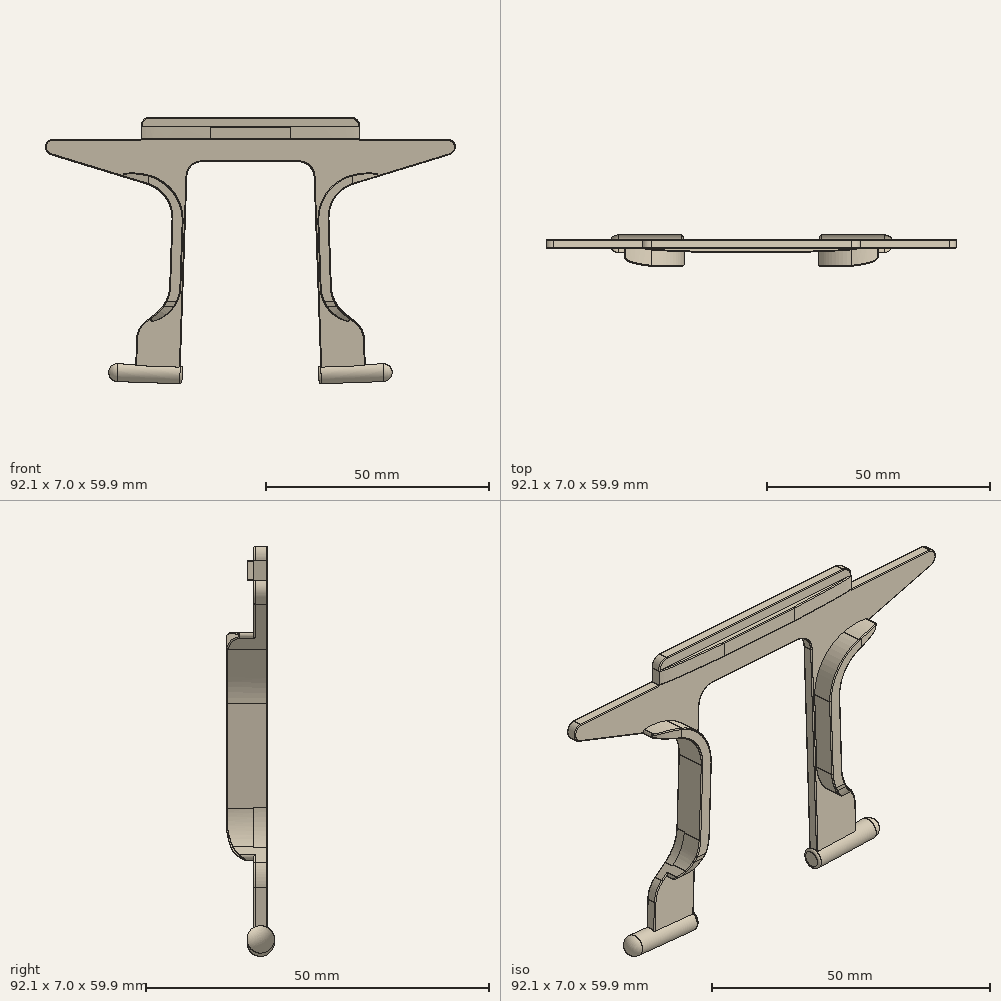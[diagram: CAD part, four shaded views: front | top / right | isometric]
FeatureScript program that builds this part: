
annotation { "Feature Type Name" : "Feature", "Feature Type Description" : "" }
export const myFeature = defineFeature(function(context is Context, id is Id, definition is map)
    precondition{}
    {
        {
            var Q0;
            Q0=qCreatedBy(makeId("Front.planeOp"),FACE);
            var sketch = newSketch(context, id + "F0", { "sketchPlane" : qUnion([Q0])});
            skLineSegment(sketch, "E0", {"start": v(24.5, 40.36) * mm, "end": v(44.5, 40.36) * mm});
            skLineSegment(sketch, "E1", {"start": v(0, 45.36) * mm, "end": v(22.5, 45.36) * mm});
            skLineSegment(sketch, "E2", {"start": v(24.5, 43.36) * mm, "end": v(24.5, 40.36) * mm});
            skPoint(sketch, "E3.visualSharp", {"position": v(24.5, 45.36) * mm});
            skArc(sketch, "E3.filletArc", {"start": v(24.5, 43.36) * mm, "mid": v(23.91, 44.77) * mm, "end": v(22.5, 45.36) * mm});
            skArc(sketch, "E4", {"start": v(44.8, 36.95) * mm, "mid": v(46, 38.99) * mm, "end": v(44.07, 40.36) * mm});
            skLineSegment(sketch, "E5", {"start": v(15.84, -12.5) * mm, "end": v(14.29, 31.98) * mm});
            skLineSegment(sketch, "E6", {"start": v(10.79, 35.36) * mm, "end": v(0, 35.36) * mm});
            skLineSegment(sketch, "E7", {"start": v(44.8, 36.95) * mm, "end": v(23.28, 30.37) * mm});
            skLineSegment(sketch, "E8", {"start": v(25.83, -12.14) * mm, "end": v(25.56, -4.43) * mm});
            skPoint(sketch, "E9.visualSharp", {"position": v(14.17, 35.36) * mm});
            skArc(sketch, "E9.filletArc", {"start": v(14.29, 31.98) * mm, "mid": v(13.22, 34.38) * mm, "end": v(10.79, 35.36) * mm});
            skLineSegment(sketch, "E10", {"start": v(25.83, -12.14) * mm, "end": v(15.84, -12.5) * mm});
            skPoint(sketch, "E11.MirrorCS.start.orphan", {"position": v(0, 45.36) * mm});
            skPoint(sketch, "E12.MirrorCS.end.orphan", {"position": v(0, 35.36) * mm});
            skLineSegment(sketch, "E13", {"start": v(0, 45.36) * mm, "end": v(0, 35.36) * mm});
            skLineSegment(sketch, "E14", {"start": v(18.06, 9.74) * mm, "end": v(17.62, 22.44) * mm});
            skPoint(sketch, "E15.visualSharp", {"position": v(17.4, 28.58) * mm});
            skArc(sketch, "E15.filletArc", {"start": v(23.28, 30.37) * mm, "mid": v(19.1, 27.37) * mm, "end": v(17.62, 22.44) * mm});
            skLineSegment(sketch, "E16", {"start": v(18.06, 9.74) * mm, "end": v(18.15, 7.33) * mm});
            skLineSegment(sketch, "E17", {"start": v(23.7, -0.71) * mm, "end": v(21.12, 1.38) * mm});
            skPoint(sketch, "E18.visualSharp", {"position": v(18.28, 3.68) * mm});
            skArc(sketch, "E18.filletArc", {"start": v(18.15, 7.33) * mm, "mid": v(18.99, 4.03) * mm, "end": v(21.12, 1.38) * mm});
            skPoint(sketch, "E19.visualSharp", {"position": v(25.48, -2.15) * mm});
            skArc(sketch, "E19.filletArc", {"start": v(25.56, -4.43) * mm, "mid": v(25.04, -2.37) * mm, "end": v(23.7, -0.71) * mm});
            skSolve(sketch);
        }
        {
            var Q0;
            Q0=makeQuery(id+"F0.imprint","IMPRINT",FACE,{"disambiguationData":[TD([[makeQuery(id+"F0.imprint","IMPRINT",EDGE,{"derivedFrom":sQuery(id+"F0.wireOp",EDGE,"E1")}),-1.0]])]});
            extrude(context, id + "F1", {"entities" : qUnion([Q0]), "depth" : 1 * mm});
        }
        {
            var Q0;
            Q0=makeQuery(id+"F1.opExtrude","SWEPT_FACE",FACE,{"disambiguationData":[OSD([sQuery(id+"F0.wireOp",EDGE,"E5")])]});
            cPlane(context, id + "F2", {"entities" : qUnion([Q0]), "cplaneType" : CPlaneType.OFFSET, "offset" : 1 * mm, "width" : 150 * mm, "height" : 150 * mm});
        }
        {
            var Q0;
            Q0=makeQuery(id+"F0.imprint","IMPRINT",FACE,{"disambiguationData":[TD([[makeQuery(id+"F0.imprint","IMPRINT",EDGE,{"derivedFrom":sQuery(id+"F0.wireOp",EDGE,"E1")}),-1.0]])]});
            extrude(context, id + "F3", {"entities" : qUnion([Q0]), "operationType" : NewBodyOperationType.ADD, "oppositeDirection" : true, "depth" : 1 * mm});
        }
        {
            var Q0;
            Q0=qCreatedBy(makeId("Front.planeOp"),FACE);
            var sketch = newSketch(context, id + "F4", { "sketchPlane" : qUnion([Q0])});
            skLineSegment(sketch, "E20.bottom", {"start": v(15.77, -10.5) * mm, "end": v(29.76, -10) * mm});
            skLineSegment(sketch, "E20.top", {"start": v(15.34, -12.5) * mm, "end": v(31.83, -11.93) * mm});
            skLineSegment(sketch, "E20.left", {"start": v(15.29, -11) * mm, "end": v(15.34, -12.5) * mm});
            skLineSegment(sketch, "E20.right", {"start": v(31.83, -11.93) * mm, "end": v(31.83, -11.93) * mm});
            skPoint(sketch, "E21.visualSharp", {"position": v(31.76, -9.93) * mm});
            skArc(sketch, "E21.filletArc", {"start": v(31.83, -11.93) * mm, "mid": v(31.2, -10.54) * mm, "end": v(29.76, -10) * mm});
            skPoint(sketch, "E22.visualSharp", {"position": v(15.27, -10.51) * mm});
            skArc(sketch, "E22.filletArc", {"start": v(15.77, -10.5) * mm, "mid": v(15.42, -10.65) * mm, "end": v(15.29, -11) * mm});
            skSolve(sketch);
        }
        {
            var Q0;
            Q0=makeQuery(id+"F4.imprint","IMPRINT",FACE,{"disambiguationData":[TD([[makeQuery(id+"F4.imprint","IMPRINT",EDGE,{"derivedFrom":sQuery(id+"F4.wireOp",EDGE,"E20.bottom")}),-1.0]])]});
            var Q1;
            Q1=sQuery(id+"F4.wireOp",EDGE,"E20.top");
            revolve(context, id + "F5", {"operationType" : NewBodyOperationType.ADD, "entities" : qUnion([Q0]), "axis" : qUnion([Q1]), "revolveType" : RevolveType.FULL});
        }
        {
            var Q0;
            Q0=qCreatedBy(makeId("Front.planeOp"),FACE);
            var sketch = newSketch(context, id + "F6", { "sketchPlane" : qUnion([Q0])});
            skLineSegment(sketch, "E23", {"start": v(28.06, 31.83) * mm, "end": v(23.28, 30.37) * mm});
            skLineSegment(sketch, "E24", {"start": v(17.97, 12.5) * mm, "end": v(17.62, 22.44) * mm});
            skArc(sketch, "E25.filletArc", {"start": v(23.28, 30.37) * mm, "mid": v(19.1, 27.37) * mm, "end": v(17.62, 22.44) * mm});
            skLineSegment(sketch, "E26", {"start": v(17.97, 12.5) * mm, "end": v(18.16, 7.1) * mm});
            skLineSegment(sketch, "E27", {"start": v(22.26, 0.46) * mm, "end": v(20.94, 1.53) * mm});
            skArc(sketch, "E28.filletArc", {"start": v(18.16, 7.1) * mm, "mid": v(18.94, 4) * mm, "end": v(20.94, 1.53) * mm});
            skLineSegment(sketch, "E29", {"start": v(15.12, 22.35) * mm, "end": v(15.66, 7.01) * mm});
            skLineSegment(sketch, "E30", {"start": v(17.62, 22.44) * mm, "end": v(15.12, 22.35) * mm});
            skLineSegment(sketch, "E31", {"start": v(22.56, 32.26) * mm, "end": v(22.56, 32.26) * mm});
            skLineSegment(sketch, "E32", {"start": v(15.14, 21.85) * mm, "end": v(15.12, 22.35) * mm});
            skArc(sketch, "E33.filletArc", {"start": v(22.56, 32.26) * mm, "mid": v(17.09, 28.32) * mm, "end": v(15.14, 21.85) * mm});
            skLineSegment(sketch, "E34", {"start": v(18.16, 7.1) * mm, "end": v(15.66, 7.01) * mm});
            skLineSegment(sketch, "E35", {"start": v(15.66, 7.01) * mm, "end": v(15.66, 7.01) * mm});
            skArc(sketch, "E36", {"start": v(15.66, 7.01) * mm, "mid": v(17.47, 2.23) * mm, "end": v(21.8, -0.46) * mm});
            skArc(sketch, "E37", {"start": v(21.8, -0.46) * mm, "mid": v(22.4, -0.18) * mm, "end": v(22.26, 0.46) * mm});
            skPoint(sketch, "E37.first.point", {"position": v(22.38, -0.22) * mm});
            skArc(sketch, "E38.trimOffspring", {"start": v(28.23, 32.75) * mm, "mid": v(25.37, 32.8) * mm, "end": v(22.56, 32.26) * mm});
            skLineSegment(sketch, "E39", {"start": v(28.06, 31.83) * mm, "end": v(28.3, 31.9) * mm});
            skArc(sketch, "E40", {"start": v(28.3, 31.9) * mm, "mid": v(28.6, 32.36) * mm, "end": v(28.23, 32.75) * mm});
            skPoint(sketch, "E40.second.point", {"position": v(28.3, 31.9) * mm});
            skSolve(sketch);
        }
        {
            var Q0;
            Q0=qSketchRegion(id+"F6",true);
            extrude(context, id + "F7", {"entities" : qUnion([Q0]), "operationType" : NewBodyOperationType.ADD, "depth" : 5 * mm});
        }
        {
            var Q0;
            Q0=qCreatedBy(makeId("Right.planeOp"),FACE);
            var sketch = newSketch(context, id + "F8", { "sketchPlane" : qUnion([Q0])});
            skFitSpline(sketch, "E41", {"points": [v(-4.8, 2.94) * mm, v(-3.88, 0.66) * mm, v(-2.13, -0.5) * mm], "startDerivative": vector(1.29, -4.9) * mm, "endDerivative": vector(4.1, -1.93) * mm});
            skLineSegment(sketch, "E42", {"start": v(-4.8, 2.94) * mm, "end": v(-5.4, 5.71) * mm});
            skLineSegment(sketch, "E43", {"start": v(-5.4, 5.71) * mm, "end": v(-6.33, 5.51) * mm});
            skLineSegment(sketch, "E44", {"start": v(-6.33, 5.51) * mm, "end": v(-6.33, 2.04) * mm});
            skLineSegment(sketch, "E45", {"start": v(-6.33, 2.04) * mm, "end": v(-6.33, -1.36) * mm});
            skLineSegment(sketch, "E46", {"start": v(-6.33, -1.36) * mm, "end": v(-2.06, -1.36) * mm});
            skLineSegment(sketch, "E47", {"start": v(-2.06, -1.36) * mm, "end": v(-2.13, -0.5) * mm});
            skSolve(sketch);
        }
        {
            var Q0;
            Q0=makeQuery(id+"F8.imprint","IMPRINT",FACE,{"disambiguationData":[TD([[makeQuery(id+"F8.imprint","IMPRINT",EDGE,{"derivedFrom":sQuery(id+"F8.wireOp",EDGE,"E41")}),-1.0]])]});
            extrude(context, id + "F9", {"entities" : qUnion([Q0]), "operationType" : NewBodyOperationType.REMOVE, "depth" : 25 * mm});
        }
        {
            var Q0;
            Q0=qCreatedBy(makeId("Top.planeOp"),FACE);
            var sketch = newSketch(context, id + "F10", { "sketchPlane" : qUnion([Q0])});
            skFitSpline(sketch, "E48", {"points": [v(28.64, -3.11) * mm, v(26.82, -4.28) * mm, v(21.34, -5.17) * mm, v(21.32, -5.17) * mm], "startDerivative": vector(-3.06, -3.38) * mm, "endDerivative": vector(-0.28, 0.04) * mm});
            skLineSegment(sketch, "E49", {"start": v(21.34, -5.17) * mm, "end": v(21.34, -6.23) * mm});
            skLineSegment(sketch, "E50", {"start": v(21.34, -6.23) * mm, "end": v(29, -6.23) * mm});
            skLineSegment(sketch, "E51", {"start": v(29, -6.23) * mm, "end": v(29.97, -3.8) * mm});
            skLineSegment(sketch, "E52", {"start": v(29.97, -3.8) * mm, "end": v(29.39, -3.18) * mm});
            skLineSegment(sketch, "E53", {"start": v(29.39, -3.18) * mm, "end": v(28.64, -3.11) * mm});
            skSolve(sketch);
        }
        {
            var Q0;
            {var subQ0=sQuery(id+"F10.wireOp",EDGE,"E49");Q0=makeQuery(id+"F10.imprint","IMPRINT",FACE,{"disambiguationData":[TD([[makeQuery(id+"F10.imprint","IMPRINT",EDGE,{"derivedFrom":subQ0}),1.0]])]});}
            extrude(context, id + "F11", {"entities" : qUnion([Q0]), "operationType" : NewBodyOperationType.REMOVE, "depth" : 35 * mm});
        }
        {
            var Q0;
            Q0=makeQuery(id+"F7.opExtrude","CAP_EDGE",EDGE,{"disambiguationData":[OSD([sQuery(id+"F6.wireOp",EDGE,"E33.filletArc")])],"isStart":false});
            fillet(context, id + "F12", {"entities" : qUnion([Q0]), "radius" : 0.2 * mm, "tangentPropagation" : true, "allowEdgeOverflow" : false});
        }
        {
            var Q0;
            Q0=qCreatedBy(makeId("Right.planeOp"),FACE);
            var sketch = newSketch(context, id + "F13", { "sketchPlane" : qUnion([Q0])});
            skLineSegment(sketch, "E54", {"start": v(0, 43.36) * mm, "end": v(0, 41.86) * mm});
            skLineSegment(sketch, "E55.MirrorCS", {"start": v(0, 41.1) * mm, "end": v(0, 41.86) * mm});
            skLineSegment(sketch, "E56.MirrorCS", {"start": v(-1.5, 40.36) * mm, "end": v(0, 40.36) * mm});
            skLineSegment(sketch, "E57.MirrorCS", {"start": v(-2, 41.86) * mm, "end": v(-2, 41.6) * mm});
            skLineSegment(sketch, "E58.MirrorCS", {"start": v(-1.5, 43.36) * mm, "end": v(0, 43.36) * mm});
            skLineSegment(sketch, "E59.MirrorCS", {"start": v(-2, 42.6) * mm, "end": v(-2, 42.86) * mm});
            skLineSegment(sketch, "E60", {"start": v(-2, 42.6) * mm, "end": v(-2, 41.86) * mm});
            skLineSegment(sketch, "E61", {"start": v(-2, 41.6) * mm, "end": v(-2, 40.86) * mm});
            skLineSegment(sketch, "E62", {"start": v(0, 40.36) * mm, "end": v(0, 41.1) * mm});
            skLineSegment(sketch, "E63", {"start": v(-1.5, 43.36) * mm, "end": v(-2, 43.36) * mm});
            skLineSegment(sketch, "E64", {"start": v(-2, 43.36) * mm, "end": v(-2, 42.86) * mm});
            skLineSegment(sketch, "E65", {"start": v(-2, 40.86) * mm, "end": v(-2, 40.36) * mm});
            skLineSegment(sketch, "E66", {"start": v(-2, 40.36) * mm, "end": v(-1.5, 40.36) * mm});
            skSolve(sketch);
        }
        {
            var Q0;
            {var subQ0=sQuery(id+"F0.wireOp",EDGE,"E1");Q0=makeQuery(id+"F3.boolean.opBoolean","MERGE",FACE,{"derivedFrom":[makeQuery(id+"F1.opExtrude","SWEPT_FACE",FACE,{"disambiguationData":[OSD([subQ0])]}),makeQuery(id+"F3.opExtrude","SWEPT_FACE",FACE,{"disambiguationData":[OSD([subQ0])]})]});}
            cPlane(context, id + "F14", {"entities" : qUnion([Q0]), "cplaneType" : CPlaneType.OFFSET, "offset" : 0 * mm, "width" : 150 * mm, "height" : 150 * mm});
        }
        {
            var Q0;
            Q0=qCreatedBy(id+"F14.planeOp",FACE);
            var sketch = newSketch(context, id + "F15", { "sketchPlane" : qUnion([Q0])});
            skFitSpline(sketch, "E67.MirrorCS", {"points": [v(24.5, -1) * mm, v(21.47, -1.45) * mm, v(5.2, -2.1) * mm, v(5.2, -2.1) * mm], "startDerivative": vector(-5.5, -1.5) * mm, "endDerivative": vector(0, 0.09) * mm});
            skLineSegment(sketch, "E68.MirrorCS", {"start": v(5.94, -2.88) * mm, "end": v(18.16, -2.88) * mm});
            skLineSegment(sketch, "E69.MirrorCS", {"start": v(18.16, -2.88) * mm, "end": v(22.17, -2.88) * mm});
            skLineSegment(sketch, "E70.MirrorCS", {"start": v(22.17, -2.88) * mm, "end": v(25.12, -2.55) * mm});
            skLineSegment(sketch, "E71.MirrorCS", {"start": v(25.12, -2.55) * mm, "end": v(25, -1.52) * mm});
            skLineSegment(sketch, "E72.MirrorCS", {"start": v(24.5, -1) * mm, "end": v(25, -1.52) * mm});
            skLineSegment(sketch, "E73.MirrorCS", {"start": v(5.2, -2.1) * mm, "end": v(5.94, -2.88) * mm});
            skSolve(sketch);
        }
        {
            var Q0;
            Q0=makeQuery(id+"F13.imprint","IMPRINT",FACE,{"disambiguationData":[TD([[makeQuery(id+"F13.imprint","IMPRINT",EDGE,{"derivedFrom":sQuery(id+"F13.wireOp",EDGE,"E54")}),-1.0]])]});
            extrude(context, id + "F16", {"entities" : qUnion([Q0]), "operationType" : NewBodyOperationType.ADD, "depth" : 24.5 * mm});
        }
        {
            var Q0;
            Q0=qSketchRegion(id+"F15",true);
            extrude(context, id + "F17", {"entities" : qUnion([Q0]), "operationType" : NewBodyOperationType.REMOVE, "oppositeDirection" : true, "depth" : 5 * mm});
        }
        {
            var Q0;
            Q0=makeQuery(id+"F1.opExtrude","CAP_EDGE",EDGE,{"disambiguationData":[OSD([sQuery(id+"F0.wireOp",EDGE,"E1")])],"isStart":false});
            var Q1;
            Q1=makeQuery(id+"F16.opExtrude","SWEPT_EDGE",EDGE,{"disambiguationData":[OSD([sQuery(id+"F13.wireOp",EDGE,"E63"),sQuery(id+"F13.wireOp",EDGE,"E64")])]});
            var Q2;
            Q2=makeQuery(id+"F1.opExtrude","CAP_EDGE",EDGE,{"disambiguationData":[OSD([sQuery(id+"F0.wireOp",EDGE,"E3.filletArc")])],"isStart":false});
            var Q3;
            Q3=makeQuery(id+"F16.opExtrude","SWEPT_EDGE",EDGE,{"disambiguationData":[OSD([sQuery(id+"F13.wireOp",EDGE,"E65"),sQuery(id+"F13.wireOp",EDGE,"E66")])]});
            var Q4;
            Q4=makeQuery(id+"F1.opExtrude","CAP_EDGE",EDGE,{"disambiguationData":[OSD([sQuery(id+"F0.wireOp",EDGE,"E6")])],"isStart":false});
            var Q5;
            Q5=makeQuery(id+"F1.opExtrude","CAP_EDGE",EDGE,{"disambiguationData":[OSD([sQuery(id+"F0.wireOp",EDGE,"E0")])],"isStart":false});
            var Q6;
            Q6=makeQuery(id+"F1.opExtrude","CAP_EDGE",EDGE,{"disambiguationData":[OSD([sQuery(id+"F0.wireOp",EDGE,"E4")])],"isStart":false});
            var Q7;
            {var subQ0=sQuery(id+"F0.wireOp",EDGE,"E7");Q7=makeQuery(id+"F11.boolean.opBoolean","INTERSECT",EDGE,{"derivedFrom":[makeQuery(id+"F7.boolean.opBoolean","MERGE",FACE,{"derivedFrom":[makeQuery(id+"F3.boolean.opBoolean","MERGE",FACE,{"derivedFrom":[makeQuery(id+"F1.opExtrude","SWEPT_FACE",FACE,{"disambiguationData":[OSD([subQ0])]}),makeQuery(id+"F3.opExtrude","SWEPT_FACE",FACE,{"disambiguationData":[OSD([subQ0])]})]}),makeQuery(id+"F7.opExtrude","SWEPT_FACE",FACE,{"disambiguationData":[OSD([sQuery(id+"F6.wireOp",EDGE,"E23"),sQuery(id+"F6.wireOp",EDGE,"E39")])]})]}),makeQuery(id+"F11.opExtrude","SWEPT_FACE",FACE,{"disambiguationData":[OSD([sQuery(id+"F10.wireOp",EDGE,"E48")])]})]});}
            var Q8;
            Q8=makeQuery(id+"F7.opExtrude","CAP_EDGE",EDGE,{"disambiguationData":[OSD([sQuery(id+"F6.wireOp",EDGE,"E25.filletArc")])],"isStart":false});
            var Q9;
            Q9=makeQuery(id+"F7.opExtrude","CAP_EDGE",EDGE,{"disambiguationData":[OSD([sQuery(id+"F6.wireOp",EDGE,"E29"),sQuery(id+"F6.wireOp",EDGE,"E32")])],"isStart":false});
            var Q10;
            Q10=makeQuery(id+"F9.boolean.opBoolean","INTERSECT",EDGE,{"derivedFrom":[makeQuery(id+"F7.opExtrude","SWEPT_FACE",FACE,{"disambiguationData":[OSD([sQuery(id+"F6.wireOp",EDGE,"E28.filletArc")])]}),makeQuery(id+"F9.opExtrude","SWEPT_FACE",FACE,{"disambiguationData":[OSD([sQuery(id+"F8.wireOp",EDGE,"E42")])]})]});
            var Q11;
            {var subQ0=sQuery(id+"F0.wireOp",EDGE,"E17");Q11=makeQuery(id+"F9.boolean.opBoolean","INTERSECT",EDGE,{"derivedFrom":[makeQuery(id+"F7.boolean.opBoolean","MERGE",FACE,{"derivedFrom":[makeQuery(id+"F3.boolean.opBoolean","MERGE",FACE,{"derivedFrom":[makeQuery(id+"F1.opExtrude","SWEPT_FACE",FACE,{"disambiguationData":[OSD([subQ0])]}),makeQuery(id+"F3.opExtrude","SWEPT_FACE",FACE,{"disambiguationData":[OSD([subQ0])]})]}),makeQuery(id+"F7.opExtrude","SWEPT_FACE",FACE,{"disambiguationData":[OSD([sQuery(id+"F6.wireOp",EDGE,"E27")])]})]}),makeQuery(id+"F9.opExtrude","SWEPT_FACE",FACE,{"disambiguationData":[OSD([sQuery(id+"F8.wireOp",EDGE,"E41")])]})]});}
            var Q12;
            Q12=makeQuery(id+"F9.boolean.opBoolean","INTERSECT",EDGE,{"derivedFrom":[makeQuery(id+"F7.opExtrude","SWEPT_FACE",FACE,{"disambiguationData":[OSD([sQuery(id+"F6.wireOp",EDGE,"E36")])]}),makeQuery(id+"F9.opExtrude","SWEPT_FACE",FACE,{"disambiguationData":[OSD([sQuery(id+"F8.wireOp",EDGE,"E41")])]})]});
            var Q13;
            Q13=makeQuery(id+"F9.boolean.opBoolean","INTERSECT",EDGE,{"derivedFrom":[makeQuery(id+"F7.opExtrude","SWEPT_FACE",FACE,{"disambiguationData":[OSD([sQuery(id+"F6.wireOp",EDGE,"E36")])]}),makeQuery(id+"F9.opExtrude","SWEPT_FACE",FACE,{"disambiguationData":[OSD([sQuery(id+"F8.wireOp",EDGE,"E42")])]})]});
            var Q14;
            Q14=makeQuery(id+"F1.opExtrude","CAP_EDGE",EDGE,{"disambiguationData":[OSD([sQuery(id+"F0.wireOp",EDGE,"E19.filletArc")])],"isStart":false});
            var Q15;
            Q15=makeQuery(id+"F1.opExtrude","CAP_EDGE",EDGE,{"disambiguationData":[OSD([sQuery(id+"F0.wireOp",EDGE,"E17")])],"isStart":false});
            var Q16;
            Q16=makeQuery(id+"F1.opExtrude","CAP_EDGE",EDGE,{"disambiguationData":[OSD([sQuery(id+"F0.wireOp",EDGE,"E8")])],"isStart":false});
            var Q17;
            Q17=makeQuery(id+"F3.opExtrude","CAP_EDGE",EDGE,{"disambiguationData":[OSD([sQuery(id+"F0.wireOp",EDGE,"E5")])],"isStart":false});
            var Q18;
            Q18=makeQuery(id+"F3.opExtrude","CAP_EDGE",EDGE,{"disambiguationData":[OSD([sQuery(id+"F0.wireOp",EDGE,"E1")])],"isStart":false});
            var Q19;
            Q19=makeQuery(id+"F3.opExtrude","CAP_EDGE",EDGE,{"disambiguationData":[OSD([sQuery(id+"F0.wireOp",EDGE,"E0")])],"isStart":false});
            var Q20;
            Q20=makeQuery(id+"F3.opExtrude","CAP_EDGE",EDGE,{"disambiguationData":[OSD([sQuery(id+"F0.wireOp",EDGE,"E4")])],"isStart":false});
            fillet(context, id + "F18", {"entities" : qUnion([Q0, Q1, Q2, Q3, Q4, Q5, Q6, Q7, Q8, Q9, Q10, Q11, Q12, Q13, Q14, Q15, Q16, Q17, Q18, Q19, Q20]), "radius" : 0.2 * mm, "tangentPropagation" : true, "allowEdgeOverflow" : false});
        }
        {
            var Q0;
            Q0=makeQuery(id+"F17.boolean.opBoolean","INTERSECT",EDGE,{"derivedFrom":[makeQuery(id+"F16.opExtrude","SWEPT_FACE",FACE,{"disambiguationData":[OSD([sQuery(id+"F13.wireOp",EDGE,"E58.MirrorCS"),sQuery(id+"F13.wireOp",EDGE,"E63")])]}),makeQuery(id+"F17.opExtrude","SWEPT_FACE",FACE,{"disambiguationData":[OSD([sQuery(id+"F15.wireOp",EDGE,"E67.MirrorCS")])]})]});
            var Q1;
            Q1=makeQuery(id+"F17.boolean.opBoolean","COPY",EDGE,{"derivedFrom":makeQuery(id+"F17.opExtrude","CAP_EDGE",EDGE,{"disambiguationData":[OSD([sQuery(id+"F15.wireOp",EDGE,"E67.MirrorCS")])],"isStart":false})});
            fillet(context, id + "F19", {"entities" : qUnion([Q0, Q1]), "radius" : 0.19 * mm, "tangentPropagation" : true, "allowEdgeOverflow" : false});
        }
        {
            var Q0;
            Q0=makeQuery(id+"F1.opExtrude","SWEPT_BODY",BODY,{"disambiguationData":[OSD([sQuery(id+"F0.wireOp",EDGE,"E0"),sQuery(id+"F0.wireOp",EDGE,"E1"),sQuery(id+"F0.wireOp",EDGE,"E2"),sQuery(id+"F0.wireOp",EDGE,"E3.filletArc"),sQuery(id+"F0.wireOp",EDGE,"E4"),sQuery(id+"F0.wireOp",EDGE,"E5"),sQuery(id+"F0.wireOp",EDGE,"E6"),sQuery(id+"F0.wireOp",EDGE,"E7"),sQuery(id+"F0.wireOp",EDGE,"E8"),sQuery(id+"F0.wireOp",EDGE,"E9.filletArc"),sQuery(id+"F0.wireOp",EDGE,"E10"),sQuery(id+"F0.wireOp",EDGE,"E13"),sQuery(id+"F0.wireOp",EDGE,"E14"),sQuery(id+"F0.wireOp",EDGE,"E15.filletArc"),sQuery(id+"F0.wireOp",EDGE,"E16"),sQuery(id+"F0.wireOp",EDGE,"E17"),sQuery(id+"F0.wireOp",EDGE,"E18.filletArc"),sQuery(id+"F0.wireOp",EDGE,"E19.filletArc")])]});
            var Q1;
            {var subQ0=sQuery(id+"F0.wireOp",EDGE,"E13");Q1=makeQuery(id+"F16.boolean.opBoolean","MERGE",FACE,{"derivedFrom":[makeQuery(id+"F3.boolean.opBoolean","MERGE",FACE,{"derivedFrom":[makeQuery(id+"F1.opExtrude","SWEPT_FACE",FACE,{"disambiguationData":[OSD([subQ0])]}),makeQuery(id+"F3.opExtrude","SWEPT_FACE",FACE,{"disambiguationData":[OSD([subQ0])]})]}),makeQuery(id+"F16.opExtrude","CAP_FACE",FACE,{"disambiguationData":[OSD([sQuery(id+"F13.wireOp",EDGE,"E54"),sQuery(id+"F13.wireOp",EDGE,"E55.MirrorCS"),sQuery(id+"F13.wireOp",EDGE,"E56.MirrorCS"),sQuery(id+"F13.wireOp",EDGE,"E57.MirrorCS"),sQuery(id+"F13.wireOp",EDGE,"E59.MirrorCS"),sQuery(id+"F13.wireOp",EDGE,"E58.MirrorCS"),sQuery(id+"F13.wireOp",EDGE,"E60"),sQuery(id+"F13.wireOp",EDGE,"E61"),sQuery(id+"F13.wireOp",EDGE,"E62"),sQuery(id+"F13.wireOp",EDGE,"E63"),sQuery(id+"F13.wireOp",EDGE,"E64"),sQuery(id+"F13.wireOp",EDGE,"E65"),sQuery(id+"F13.wireOp",EDGE,"E66")])],"isStart":true})]});}
            mirror(context, id + "F20", {"operationType" : NewBodyOperationType.ADD, "entities" : qUnion([Q0]), "mirrorPlane" : qUnion([Q1])});
        }
    });
